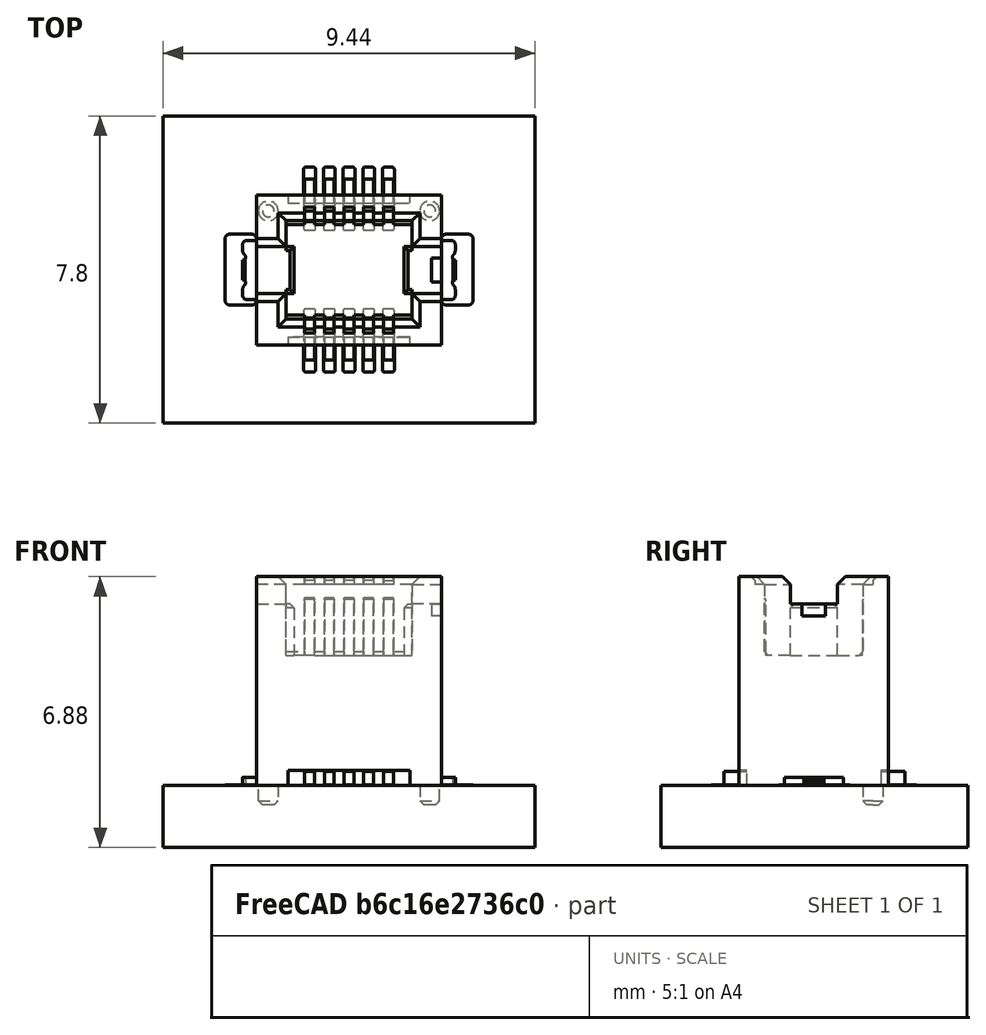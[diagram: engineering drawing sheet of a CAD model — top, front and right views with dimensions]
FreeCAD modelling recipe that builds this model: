
FCSTD DOCUMENT  (FreeCAD 1.0R39285 (Git))
Label: 10132797-017100LF
License: All rights reserved
LicenseURL: https://en.wikipedia.org/wiki/All_rights_reserved
objects: Part::Feature×6, Sketcher::SketchObject×3, App::DocumentObjectGroup×1
note: 12 computed .brp shape members not serialized (recipe doc carries the construction recipe); baked Part::Feature solids carry a one-line shape summary decoded from their .brp

FEATURE [Part::Feature] Shape001  label="topPads"
  Placement = pos=(0,0,-0.01) rot=(0,0,1;0rad)
  shape: bbox 6.3 x 5.2 x 0.01 mm, 120 faces, 12 solids (baked)
FEATURE [Part::Feature] Shape  label="F.SilkS_outline_"
  Placement = pos=(0,0,0.01) rot=(0,0,1;0rad)
  shape: bbox 4.8 x 0.4 x 2e-07 mm, 0 faces, 0 solids (baked)
FEATURE [Sketcher::SketchObject] _F_SilkS__sketch  label="F.SilkS_"
  ArcFitTolerance = 1e-06
  FullyConstrained = false
  MakeInternals = false
  Placement = pos=(0,0,0.01) rot=(0,0,1;0rad)
  sketch-geometry (4):
    g0: LineSegment StartX=-2.35 StartY=-1.9 StartZ=0 EndX=-2.35 EndY=-1.6 EndZ=0
    g1: LineSegment StartX=-2.35 StartY=-1.9 StartZ=0 EndX=-2.05 EndY=-1.9 EndZ=0
    g2: LineSegment StartX=2.35 StartY=-1.9 StartZ=0 EndX=2.05 EndY=-1.9 EndZ=0
    g3: LineSegment StartX=2.35 StartY=-1.9 StartZ=0 EndX=2.35 EndY=-1.6 EndZ=0
FEATURE [Part::Feature] Shape002  label="F.Fab_outline_"
  Placement = pos=(0,0,0.01) rot=(0,0,1;0rad)
  shape: bbox 4.8 x 3.9 x 2e-07 mm, 0 faces, 0 solids (baked)
FEATURE [Sketcher::SketchObject] _F_Fab__sketch  label="F.Fab_"
  ArcFitTolerance = 1e-06
  FullyConstrained = false
  MakeInternals = false
  Placement = pos=(0,0,0.01) rot=(0,0,1;0rad)
  sketch-geometry (4):
    g0: LineSegment StartX=-2.35 StartY=1.9 StartZ=0 EndX=-2.35 EndY=-1.9 EndZ=0
    g1: LineSegment StartX=-2.35 StartY=-1.9 StartZ=0 EndX=2.35 EndY=-1.9 EndZ=0
    g2: LineSegment StartX=2.35 StartY=-1.9 StartZ=0 EndX=2.35 EndY=1.9 EndZ=0
    g3: LineSegment StartX=2.35 StartY=1.9 StartZ=0 EndX=-2.35 EndY=1.9 EndZ=0
  constraints (4):
    c: Coincident(g0,g1)
    c: Coincident(g1,g2)
    c: Coincident(g2,g3)
    c: Coincident(g3,g0)
FEATURE [Part::Feature] Shape003  label="Edge.Cuts_outline_"
  Placement = pos=(0,0,0.01) rot=(0,0,1;0rad)
  shape: bbox 4.85 x 0.75 x 2e-07 mm, 0 faces, 0 solids (baked)
FEATURE [Sketcher::SketchObject] _Edge_Cuts__sketch  label="Edge.Cuts_"
  ArcFitTolerance = 1e-06
  FullyConstrained = false
  MakeInternals = false
  Placement = pos=(0,0,0.01) rot=(0,0,1;0rad)
  sketch-geometry (2):
    g0: Circle CenterX=-2.05 CenterY=1.5 CenterZ=0 NormalX=0 NormalY=0 NormalZ=1 AngleXU=0 Radius=0.35
    g1: Circle CenterX=2.05 CenterY=1.5 CenterZ=0 NormalX=0 NormalY=0 NormalZ=1 AngleXU=0 Radius=0.35
FEATURE [Part::Feature] PCB
  shape: bbox 9.45 x 7.8 x 1.58 mm, 6 faces (baked)
FEATURE [App::DocumentObjectGroup] Group  label="10132797-017100LF-fp"
  Group = -> [Shape001,_F_SilkS__sketch,Shape,_F_Fab__sketch,Shape002,_Edge_Cuts__sketch,Shape003,PCB]
FEATURE [Part::Feature] Shape081  label="10132797-017100LF"
  shape: bbox 5.4 x 4.6 x 5.8 mm, 279 faces (baked)
